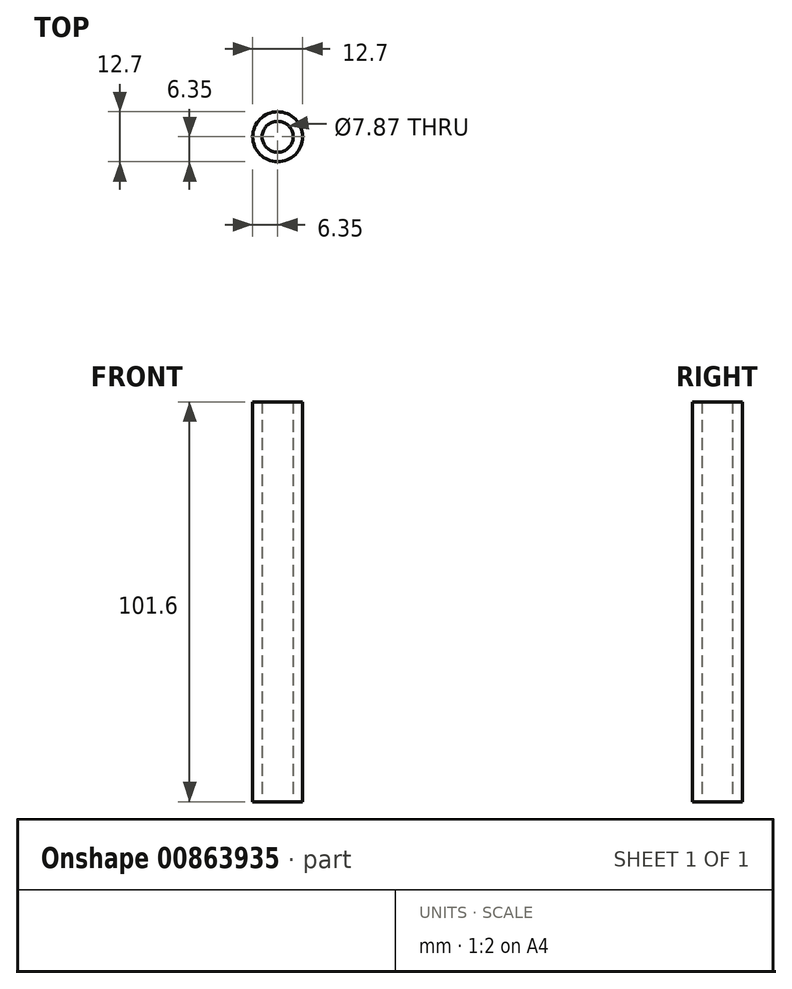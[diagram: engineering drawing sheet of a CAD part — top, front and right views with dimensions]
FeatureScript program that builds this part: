
annotation { "Feature Type Name" : "Feature", "Feature Type Description" : "" }
export const myFeature = defineFeature(function(context is Context, id is Id, definition is map)
    precondition{}
    {
        {
            var Q0;
            Q0=qCreatedBy(makeId("Top.planeOp"),FACE);
            var sketch = newSketch(context, id + "F0", { "sketchPlane" : qUnion([Q0])});
            skCircle(sketch, "E0", {"center": v(0, 0) * mm, "radius": 6.35 * mm});
            skCircle(sketch, "E1", {"center": v(0, 0) * mm, "radius": 3.94 * mm});
            skSolve(sketch);
        }
        {
            var Q0;
            Q0=makeQuery(id+"F0.imprint","IMPRINT",FACE,{"disambiguationData":[TD([[makeQuery(id+"F0.imprint","IMPRINT",EDGE,{"derivedFrom":sQuery(id+"F0.wireOp",EDGE,"E0")}),1.0]])]});
            extrude(context, id + "F1", {"entities" : qUnion([Q0]), "depth" : 101.6 * mm, "offsetDistance" : 25.4 * mm});
        }
    });
